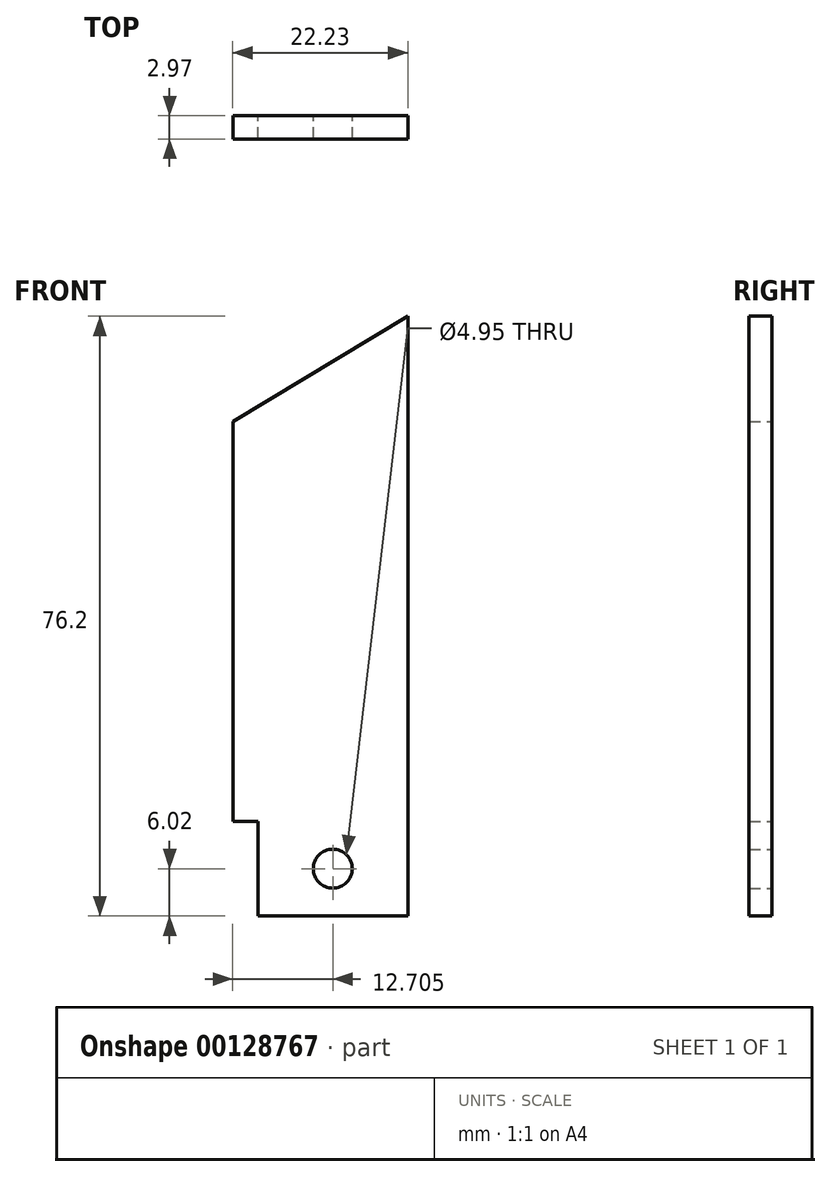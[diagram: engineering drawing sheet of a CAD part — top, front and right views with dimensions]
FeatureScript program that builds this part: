
annotation { "Feature Type Name" : "Feature", "Feature Type Description" : "" }
export const myFeature = defineFeature(function(context is Context, id is Id, definition is map)
    precondition{}
    {
        {
            var Q0;
            Q0=qCreatedBy(makeId("Front.planeOp"),FACE);
            var sketch = newSketch(context, id + "F0", { "sketchPlane" : qUnion([Q0])});
            skLineSegment(sketch, "E0", {"start": v(0, 0) * mm, "end": v(0, 76.2) * mm});
            skLineSegment(sketch, "E1", {"start": v(0, 76.2) * mm, "end": v(-22.23, 62.84) * mm});
            skLineSegment(sketch, "E2", {"start": v(-22.23, 62.84) * mm, "end": v(-22.23, 12.04) * mm});
            skLineSegment(sketch, "E3", {"start": v(-22.23, 12.04) * mm, "end": v(-19.05, 12.04) * mm});
            skLineSegment(sketch, "E4", {"start": v(-19.05, 12.04) * mm, "end": v(-19.05, 0) * mm});
            skLineSegment(sketch, "E5", {"start": v(-19.05, 0) * mm, "end": v(0, 0) * mm});
            skCircle(sketch, "E6", {"center": v(-9.53, 6.02) * mm, "radius": 2.48 * mm});
            skPoint(sketch, "E7", {"position": v(-9.53, 0) * mm});
            skSolve(sketch);
        }
        {
            var Q0;
            Q0 = qSketchRegion(id + "F0", true);
            extrude(context, id + "F1", {"entities" : qUnion([Q0]), "depth" : 2.97 * mm});
        }
    });
